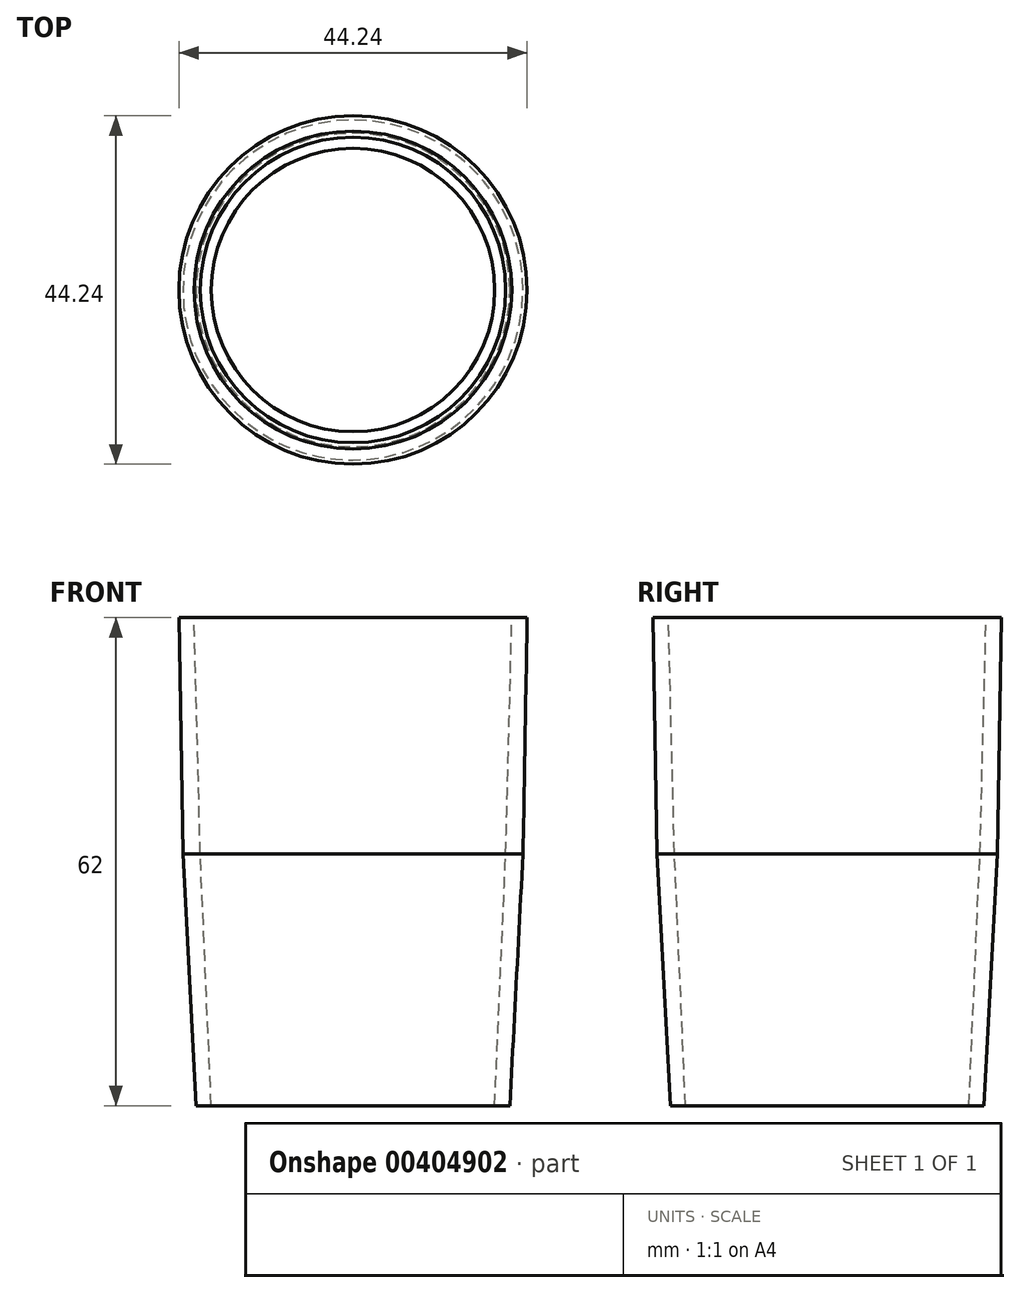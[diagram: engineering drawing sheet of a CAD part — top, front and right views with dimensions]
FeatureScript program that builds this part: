
annotation { "Feature Type Name" : "Feature", "Feature Type Description" : "" }
export const myFeature = defineFeature(function(context is Context, id is Id, definition is map)
    precondition{}
    {
        {
            var Q0;
            Q0=qCreatedBy(makeId("Top.planeOp"),FACE);
            var sketch = newSketch(context, id + "F0", { "sketchPlane" : qUnion([Q0]), "disableImprinting" : false});
            skCircle(sketch, "E0", {"center": v(0, 0) * mm, "radius": 21.6 * mm});
            skCircle(sketch, "E1", {"center": v(0, 0) * mm, "radius": 19.4 * mm});
            skSolve(sketch);
        }
        {
            var Q0;
            Q0 = qSketchRegion(id + "F0", true);
            var Q1;
            Q1=makeQuery(id+"F0.imprint","IMPRINT",FACE,{"disambiguationData":[TD([[makeQuery(id+"F0.imprint","IMPRINT",EDGE,{"derivedFrom":sQuery(id+"F0.wireOp",EDGE,"E1")}),1.0]])]});
            extrude(context, id + "F1", {"entities" : qUnion([Q0, Q1]), "flatOperationType" : FlatOperationType.REMOVE, "oppositeDirection" : true, "depth" : 32 * mm, "offsetDistance" : 25 * mm, "hasDraft" : true, "draftAngle" : 3 * degree, "draftPullDirection" : true, "domain" : OperationDomain.MODEL});
        }
        {
            var Q0;
            Q0=makeQuery(id+"F0.imprint","IMPRINT",FACE,{"disambiguationData":[TD([[makeQuery(id+"F0.imprint","IMPRINT",EDGE,{"derivedFrom":sQuery(id+"F0.wireOp",EDGE,"E1")}),1.0]])]});
            extrude(context, id + "F2", {"entities" : qUnion([Q0]), "operationType" : NewBodyOperationType.REMOVE, "flatOperationType" : FlatOperationType.REMOVE, "oppositeDirection" : true, "depth" : 40 * mm, "offsetDistance" : 25 * mm, "hasDraft" : true, "draftAngle" : 2.5 * degree, "draftPullDirection" : true, "domain" : OperationDomain.MODEL});
        }
        {
            var Q0;
            Q0=makeQuery(id+"F0.imprint","IMPRINT",FACE,{"disambiguationData":[TD([[makeQuery(id+"F0.imprint","IMPRINT",EDGE,{"derivedFrom":sQuery(id+"F0.wireOp",EDGE,"E0")}),1.0]])]});
            extrude(context, id + "F3", {"entities" : qUnion([Q0]), "operationType" : NewBodyOperationType.ADD, "flatOperationType" : FlatOperationType.REMOVE, "depth" : 30 * mm, "offsetDistance" : 25 * mm, "hasDraft" : true, "draftAngle" : 1 * degree, "domain" : OperationDomain.MODEL});
        }
        {
            var Q0;
            Q0=makeQuery(id+"F0.imprint","IMPRINT",FACE,{"disambiguationData":[TD([[makeQuery(id+"F0.imprint","IMPRINT",EDGE,{"derivedFrom":sQuery(id+"F0.wireOp",EDGE,"E1")}),1.0]])]});
            extrude(context, id + "F4", {"entities" : qUnion([Q0]), "operationType" : NewBodyOperationType.REMOVE, "flatOperationType" : FlatOperationType.REMOVE, "depth" : 35 * mm, "offsetDistance" : 25 * mm, "hasDraft" : true, "draftAngle" : 1.5 * degree, "domain" : OperationDomain.MODEL});
        }
    });
